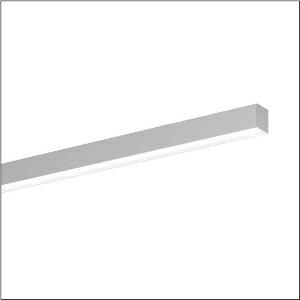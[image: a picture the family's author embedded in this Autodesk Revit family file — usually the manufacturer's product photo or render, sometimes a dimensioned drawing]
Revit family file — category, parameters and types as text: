
# Revit family: silica_r__21_51mx20tbt2s_686e
name_source: partatom
category: Lighting Fixtures
units: mm (PartAtom-declared; Revit-internal decimal feet)

## family parameters
Cut with Voids When Loaded = No
Host = Face
Light Source = No
Part Type = Normal
Room Calculation Point = No
Round Connector Dimension = Use Diameter
Shared = No

## types (1)
- --- (1 x LED, 3000 lm, 25.6 W, 6500K)
    Apparent Load = 26 VA
    CIE Flux Codes = 48 79 96 100 100
    Color Rendering = 80
    Color Temperature = 6500K
    Default Elevation = 1800 mm
    Description = Silica® 21, office luminaire, primary optical cover: cover, of PMMA, opal, light emission: direct distribution, primary light characteristic: symmetric, installation type: surface-mounted, LED, rated luminous flux: 3.000lm, luminous efficacy: 112lm/W, light colour: 8tw, colour temperature: 2700..6500K, control gear: ECG DALI, with terminal, 3+2-pole, max. 2.5mm², mains connection: 220..240V, AC, 50/60Hz, rated input power: 26.9W, luminaire housing, of aluminium, metallic grey (RAL 9006), length: 1.504mm, width: 53mm, height: 53mm, protection rating (complete): IP20, insulation class (complete): insulation class I (protective earthing), certification: CE, permissible operating ambient temperature: 0..+35°C, standard: EN 50419, packaging unit: 1 piece
    Height = 0 mm  [stored 0 ft]
    Lamp = 1 x LED
    Lamp Light Flux = 3000 lm
    Lamp Power = 25.6 W
    Lamp count = 1
    Length = 1504 mm
    Luminous efficacy = 117 lm/W
    Manufacturer = Siteco
    ModVariant = No
    Model = 51MX20TBT2S
    Mounting Place = Ceiling
    Mounting Type = Recessed
    Number of Poles = 1
    OnlyDefault = Yes
    Power Factor = 1
    Product Name = Silica® 21
    Product group = office luminaire | ceiling recessed
    ProductGroupID = 401
    Protection Class = Protection class I
    Protection Degree = IP 20
    RLX_Detail_Level = 1
    RLX_Emergency_Light_Flux = 0 lm
    RLX_Emergency_Type = 0
    RLX_Emergency_Type_DB = No
    RlxData = <blob elided: 23189 chars, md5=98a10cae>
    Socket = socket
    Standby Power = 0 W
    System Light Flux = 3000 lm
    System Power = 26 W
    Type Comments = individual setting
    Type Image = l_1313588.jpg
    URL = http://relux.com
    VarID = @adj_089037
    Voltage = 0 V
    Weight = 0.00 kg
    Width = 53 mm

note: [stored X ft] marks values corroborated as IEEE doubles in the binary element streams (Revit-internal decimal feet)

## geometry (parser evidence)
native form markers: Blend x4, Sweep x11
no freeform markers — native parametric forms only
